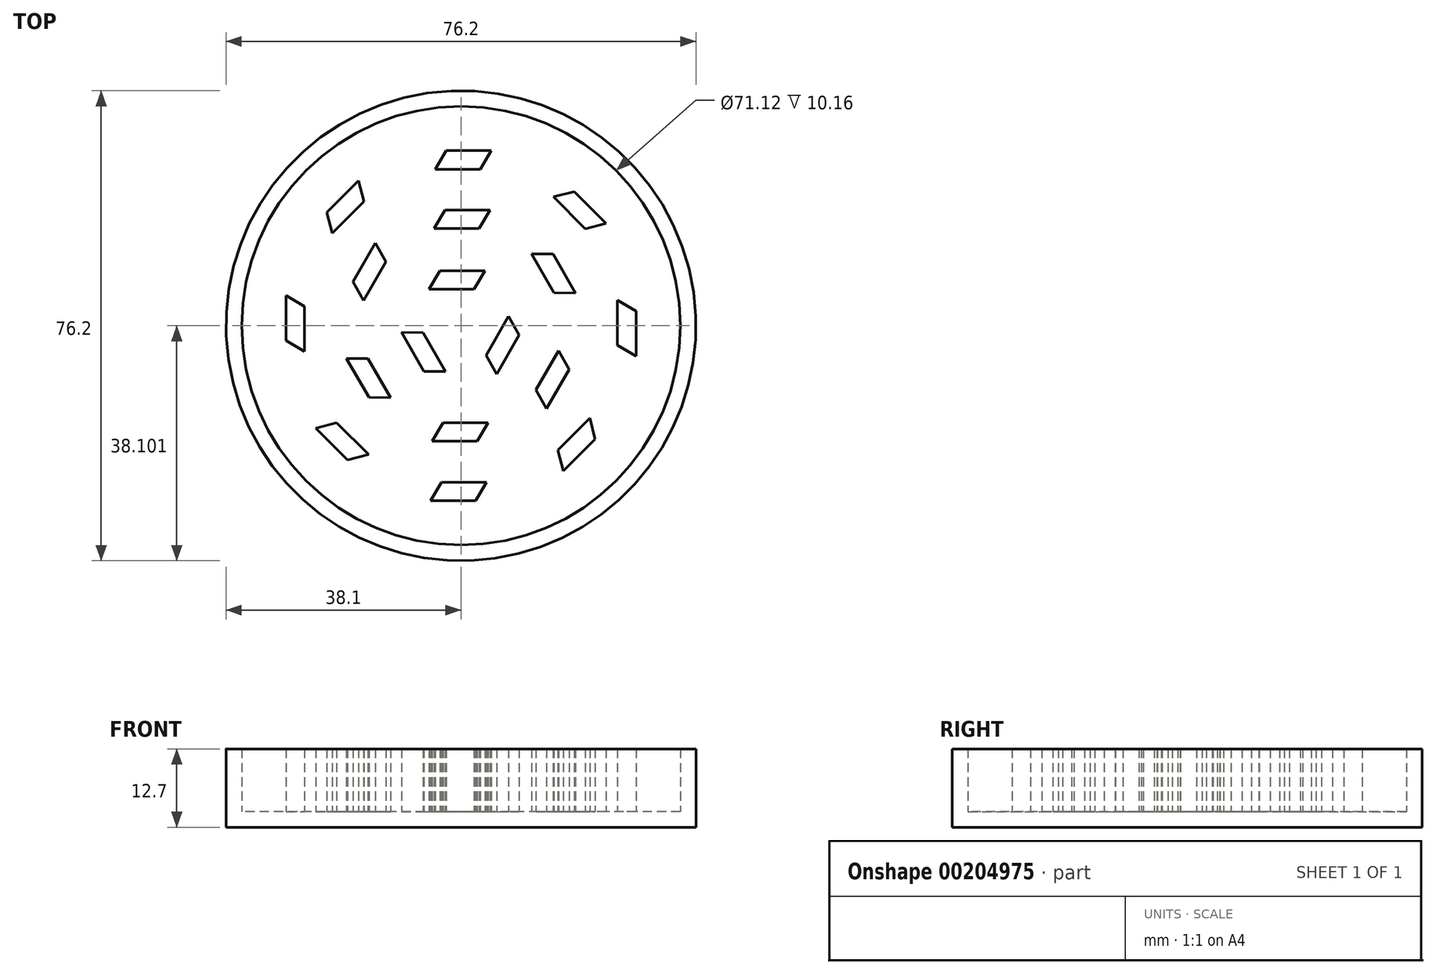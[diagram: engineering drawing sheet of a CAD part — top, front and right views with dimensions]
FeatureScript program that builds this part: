
annotation { "Feature Type Name" : "Feature", "Feature Type Description" : "" }
export const myFeature = defineFeature(function(context is Context, id is Id, definition is map)
    precondition{}
    {
        {
            var Q0;
            Q0=qCreatedBy(makeId("Top.planeOp"),FACE);
            var sketch = newSketch(context, id + "F0", { "sketchPlane" : qUnion([Q0])});
            skCircle(sketch, "E0", {"center": v(0, 0) * mm, "radius": 38.1 * mm});
            skSolve(sketch);
        }
        {
            var Q0;
            Q0=makeQuery(id+"F0.imprint","IMPRINT",FACE,{"disambiguationData":[TD([[makeQuery(id+"F0.imprint","IMPRINT",EDGE,{"derivedFrom":sQuery(id+"F0.wireOp",EDGE,"E0")}),1.0]])]});
            extrude(context, id + "F1", {"entities" : qUnion([Q0]), "oppositeDirection" : true, "depth" : 2.54 * mm});
        }
        {
            var Q0;
            Q0=makeQuery(id+"F1.opExtrude","CAP_FACE",FACE,{"disambiguationData":[OSD([sQuery(id+"F0.wireOp",EDGE,"E0")])],"isStart":true});
            var sketch = newSketch(context, id + "F2", { "sketchPlane" : qUnion([Q0])});
            skCircle(sketch, "E1", {"center": v(0, 0) * mm, "radius": 38.1 * mm});
            skCircle(sketch, "E2", {"center": v(0, 0) * mm, "radius": 35.56 * mm});
            skCircle(sketch, "E3", {"center": v(0, 0) * mm, "radius": 1.65 * mm});
            skCircle(sketch, "E4.cCircle", {"center": v(0, 0) * mm, "radius": 2.43 * mm, "construction": true});
            skPoint(sketch, "E4.0.midPoint", {"position": v(2.1, -1.21) * mm});
            skCircle(sketch, "E5", {"center": v(0, 0) * mm, "radius": 5.8 * mm, "construction": true});
            skCircle(sketch, "E6.0", {"center": v(0, 0) * mm, "radius": 9.86 * mm, "construction": true});
            skCircle(sketch, "E7.0", {"center": v(0, 0) * mm, "radius": 33.02 * mm});
            skCircle(sketch, "E8.0", {"center": v(0, 0) * mm, "radius": 10.62 * mm, "construction": true});
            skCircle(sketch, "E9.0", {"center": v(0, 0) * mm, "radius": 14.69 * mm, "construction": true});
            skCircle(sketch, "E10.0", {"center": v(0, 0) * mm, "radius": 15.45 * mm, "construction": true});
            skCircle(sketch, "E11.0", {"center": v(0, 0) * mm, "radius": 19.51 * mm, "construction": true});
            skCircle(sketch, "E12.0", {"center": v(0, 0) * mm, "radius": 20.27 * mm, "construction": true});
            skCircle(sketch, "E13.0", {"center": v(0, 0) * mm, "radius": 24.34 * mm, "construction": true});
            skCircle(sketch, "E14.0", {"center": v(0, 0) * mm, "radius": 25.1 * mm, "construction": true});
            skCircle(sketch, "E15.0", {"center": v(0, 0) * mm, "radius": 29.16 * mm, "construction": true});
            skCircle(sketch, "E16.0", {"center": v(0, 0) * mm, "radius": 29.93 * mm, "construction": true});
            skLineSegment(sketch, "E17.2.0", {"start": v(2.12, 5.9) * mm, "end": v(-5.18, 5.9) * mm});
            skLineSegment(sketch, "E17.2.1", {"start": v(3.9, 8.9) * mm, "end": v(2.12, 5.9) * mm});
            skLineSegment(sketch, "E17.2.2", {"start": v(3.9, 8.9) * mm, "end": v(-3.4, 8.9) * mm});
            skLineSegment(sketch, "E17.2.3", {"start": v(-3.4, 8.9) * mm, "end": v(-5.18, 5.9) * mm});
            skLineSegment(sketch, "E18.1.0", {"start": v(-9.66, -1.08) * mm, "end": v(-6.17, -1.11) * mm});
            skLineSegment(sketch, "E18.1.1", {"start": v(-6.17, -1.11) * mm, "end": v(-2.52, -7.44) * mm});
            skLineSegment(sketch, "E18.1.2", {"start": v(-6.01, -7.4) * mm, "end": v(-2.52, -7.44) * mm});
            skLineSegment(sketch, "E18.1.3", {"start": v(-9.66, -1.08) * mm, "end": v(-6.01, -7.4) * mm});
            skLineSegment(sketch, "E18.2.0", {"start": v(5.77, -7.83) * mm, "end": v(4.05, -4.79) * mm});
            skLineSegment(sketch, "E18.2.1", {"start": v(4.05, -4.79) * mm, "end": v(7.7, 1.53) * mm});
            skLineSegment(sketch, "E18.2.2", {"start": v(9.42, -1.5) * mm, "end": v(7.7, 1.53) * mm});
            skLineSegment(sketch, "E18.2.3", {"start": v(5.77, -7.83) * mm, "end": v(9.42, -1.5) * mm});
            skLineSegment(sketch, "E19.2.0", {"start": v(2.92, 15.74) * mm, "end": v(-4.38, 15.74) * mm});
            skLineSegment(sketch, "E19.2.1", {"start": v(4.7, 18.74) * mm, "end": v(2.92, 15.74) * mm});
            skLineSegment(sketch, "E19.2.2", {"start": v(4.7, 18.74) * mm, "end": v(-2.6, 18.74) * mm});
            skLineSegment(sketch, "E19.2.3", {"start": v(-2.6, 18.74) * mm, "end": v(-4.38, 15.74) * mm});
            skLineSegment(sketch, "E20.1.0", {"start": v(-13.88, 13.44) * mm, "end": v(-12.17, 10.4) * mm});
            skLineSegment(sketch, "E20.1.1", {"start": v(-13.88, 13.44) * mm, "end": v(-17.54, 7.11) * mm});
            skLineSegment(sketch, "E20.1.2", {"start": v(-12.17, 10.4) * mm, "end": v(-15.82, 4.07) * mm});
            skLineSegment(sketch, "E20.1.3", {"start": v(-17.54, 7.11) * mm, "end": v(-15.82, 4.07) * mm});
            skLineSegment(sketch, "E20.2.0", {"start": v(-18.58, -5.3) * mm, "end": v(-15.09, -5.34) * mm});
            skLineSegment(sketch, "E20.2.1", {"start": v(-18.58, -5.3) * mm, "end": v(-14.93, -11.63) * mm});
            skLineSegment(sketch, "E20.2.2", {"start": v(-15.09, -5.34) * mm, "end": v(-11.44, -11.66) * mm});
            skLineSegment(sketch, "E20.2.3", {"start": v(-14.93, -11.63) * mm, "end": v(-11.44, -11.66) * mm});
            skLineSegment(sketch, "E20.3.0", {"start": v(-4.7, -18.74) * mm, "end": v(-2.92, -15.74) * mm});
            skLineSegment(sketch, "E20.3.1", {"start": v(-4.7, -18.74) * mm, "end": v(2.6, -18.74) * mm});
            skLineSegment(sketch, "E20.3.2", {"start": v(-2.92, -15.74) * mm, "end": v(4.38, -15.74) * mm});
            skLineSegment(sketch, "E20.3.3", {"start": v(2.6, -18.74) * mm, "end": v(4.38, -15.74) * mm});
            skLineSegment(sketch, "E20.4.0", {"start": v(13.88, -13.44) * mm, "end": v(12.17, -10.4) * mm});
            skLineSegment(sketch, "E20.4.1", {"start": v(13.88, -13.44) * mm, "end": v(17.54, -7.11) * mm});
            skLineSegment(sketch, "E20.4.2", {"start": v(12.17, -10.4) * mm, "end": v(15.82, -4.07) * mm});
            skLineSegment(sketch, "E20.4.3", {"start": v(17.54, -7.11) * mm, "end": v(15.82, -4.07) * mm});
            skLineSegment(sketch, "E20.5.0", {"start": v(18.58, 5.3) * mm, "end": v(15.09, 5.34) * mm});
            skLineSegment(sketch, "E20.5.1", {"start": v(18.58, 5.3) * mm, "end": v(14.93, 11.63) * mm});
            skLineSegment(sketch, "E20.5.2", {"start": v(15.09, 5.34) * mm, "end": v(11.44, 11.66) * mm});
            skLineSegment(sketch, "E20.5.3", {"start": v(14.93, 11.63) * mm, "end": v(11.44, 11.66) * mm});
            skLineSegment(sketch, "E21.2.0", {"start": v(3.13, 25.38) * mm, "end": v(-4.17, 25.38) * mm});
            skLineSegment(sketch, "E21.2.1", {"start": v(4.9, 28.38) * mm, "end": v(3.13, 25.38) * mm});
            skLineSegment(sketch, "E21.2.2", {"start": v(4.9, 28.38) * mm, "end": v(-2.4, 28.38) * mm});
            skLineSegment(sketch, "E21.2.3", {"start": v(-2.4, 28.38) * mm, "end": v(-4.17, 25.38) * mm});
            skLineSegment(sketch, "E22.1.0", {"start": v(-15.73, 20.16) * mm, "end": v(-20.9, 15) * mm});
            skLineSegment(sketch, "E22.1.1", {"start": v(-16.6, 23.54) * mm, "end": v(-15.73, 20.16) * mm});
            skLineSegment(sketch, "E22.1.2", {"start": v(-16.6, 23.54) * mm, "end": v(-21.76, 18.38) * mm});
            skLineSegment(sketch, "E22.1.3", {"start": v(-21.76, 18.38) * mm, "end": v(-20.9, 15) * mm});
            skLineSegment(sketch, "E22.2.0", {"start": v(-25.38, 3.13) * mm, "end": v(-25.38, -4.17) * mm});
            skLineSegment(sketch, "E22.2.1", {"start": v(-28.38, 4.9) * mm, "end": v(-25.38, 3.13) * mm});
            skLineSegment(sketch, "E22.2.2", {"start": v(-28.38, 4.9) * mm, "end": v(-28.38, -2.4) * mm});
            skLineSegment(sketch, "E22.2.3", {"start": v(-28.38, -2.4) * mm, "end": v(-25.38, -4.17) * mm});
            skLineSegment(sketch, "E22.3.0", {"start": v(-20.16, -15.73) * mm, "end": v(-15, -20.9) * mm});
            skLineSegment(sketch, "E22.3.1", {"start": v(-23.54, -16.6) * mm, "end": v(-20.16, -15.73) * mm});
            skLineSegment(sketch, "E22.3.2", {"start": v(-23.54, -16.6) * mm, "end": v(-18.38, -21.76) * mm});
            skLineSegment(sketch, "E22.3.3", {"start": v(-18.38, -21.76) * mm, "end": v(-15, -20.9) * mm});
            skLineSegment(sketch, "E22.4.0", {"start": v(-3.13, -25.38) * mm, "end": v(4.17, -25.38) * mm});
            skLineSegment(sketch, "E22.4.1", {"start": v(-4.9, -28.38) * mm, "end": v(-3.13, -25.38) * mm});
            skLineSegment(sketch, "E22.4.2", {"start": v(-4.9, -28.38) * mm, "end": v(2.4, -28.38) * mm});
            skLineSegment(sketch, "E22.4.3", {"start": v(2.4, -28.38) * mm, "end": v(4.17, -25.38) * mm});
            skLineSegment(sketch, "E22.5.0", {"start": v(15.73, -20.16) * mm, "end": v(20.9, -15) * mm});
            skLineSegment(sketch, "E22.5.1", {"start": v(16.6, -23.54) * mm, "end": v(15.73, -20.16) * mm});
            skLineSegment(sketch, "E22.5.2", {"start": v(16.6, -23.54) * mm, "end": v(21.76, -18.38) * mm});
            skLineSegment(sketch, "E22.5.3", {"start": v(21.76, -18.38) * mm, "end": v(20.9, -15) * mm});
            skLineSegment(sketch, "E22.6.0", {"start": v(25.38, -3.13) * mm, "end": v(25.38, 4.17) * mm});
            skLineSegment(sketch, "E22.6.1", {"start": v(28.38, -4.9) * mm, "end": v(25.38, -3.13) * mm});
            skLineSegment(sketch, "E22.6.2", {"start": v(28.38, -4.9) * mm, "end": v(28.38, 2.4) * mm});
            skLineSegment(sketch, "E22.6.3", {"start": v(28.38, 2.4) * mm, "end": v(25.38, 4.17) * mm});
            skLineSegment(sketch, "E22.7.0", {"start": v(20.16, 15.73) * mm, "end": v(15, 20.9) * mm});
            skLineSegment(sketch, "E22.7.1", {"start": v(23.54, 16.6) * mm, "end": v(20.16, 15.73) * mm});
            skLineSegment(sketch, "E22.7.2", {"start": v(23.54, 16.6) * mm, "end": v(18.38, 21.76) * mm});
            skLineSegment(sketch, "E22.7.3", {"start": v(18.38, 21.76) * mm, "end": v(15, 20.9) * mm});
            skSolve(sketch);
        }
        {
            var Q0;
            Q0=makeQuery(id+"F2.imprint","IMPRINT",FACE,{"disambiguationData":[TD([[makeQuery(id+"F2.imprint","IMPRINT",EDGE,{"derivedFrom":sQuery(id+"F2.wireOp",EDGE,"E2")}),-1.0]])]});
            var Q1;
            Q1=makeQuery(id+"F2.imprint","IMPRINT",FACE,{"disambiguationData":[TD([[makeQuery(id+"F2.imprint","IMPRINT",EDGE,{"derivedFrom":sQuery(id+"F2.wireOp",EDGE,"E21.2.0")}),-1.0]])]});
            var Q2;
            Q2=makeQuery(id+"F2.imprint","IMPRINT",FACE,{"disambiguationData":[TD([[makeQuery(id+"F2.imprint","IMPRINT",EDGE,{"derivedFrom":sQuery(id+"F2.wireOp",EDGE,"E22.7.0")}),-1.0]])]});
            var Q3;
            Q3=makeQuery(id+"F2.imprint","IMPRINT",FACE,{"disambiguationData":[TD([[makeQuery(id+"F2.imprint","IMPRINT",EDGE,{"derivedFrom":sQuery(id+"F2.wireOp",EDGE,"E22.6.0")}),-1.0]])]});
            var Q4;
            Q4=makeQuery(id+"F2.imprint","IMPRINT",FACE,{"disambiguationData":[TD([[makeQuery(id+"F2.imprint","IMPRINT",EDGE,{"derivedFrom":sQuery(id+"F2.wireOp",EDGE,"E20.5.0")}),-1.0]])]});
            var Q5;
            Q5=makeQuery(id+"F2.imprint","IMPRINT",FACE,{"disambiguationData":[TD([[makeQuery(id+"F2.imprint","IMPRINT",EDGE,{"derivedFrom":sQuery(id+"F2.wireOp",EDGE,"E19.2.0")}),-1.0]])]});
            var Q6;
            Q6=makeQuery(id+"F2.imprint","IMPRINT",FACE,{"disambiguationData":[TD([[makeQuery(id+"F2.imprint","IMPRINT",EDGE,{"derivedFrom":sQuery(id+"F2.wireOp",EDGE,"E22.1.0")}),-1.0]])]});
            var Q7;
            Q7=makeQuery(id+"F2.imprint","IMPRINT",FACE,{"disambiguationData":[TD([[makeQuery(id+"F2.imprint","IMPRINT",EDGE,{"derivedFrom":sQuery(id+"F2.wireOp",EDGE,"E20.1.0")}),-1.0]])]});
            var Q8;
            Q8=makeQuery(id+"F2.imprint","IMPRINT",FACE,{"disambiguationData":[TD([[makeQuery(id+"F2.imprint","IMPRINT",EDGE,{"derivedFrom":sQuery(id+"F2.wireOp",EDGE,"E17.2.0")}),-1.0]])]});
            var Q9;
            Q9=makeQuery(id+"F2.imprint","IMPRINT",FACE,{"disambiguationData":[TD([[makeQuery(id+"F2.imprint","IMPRINT",EDGE,{"derivedFrom":sQuery(id+"F2.wireOp",EDGE,"E22.2.0")}),-1.0]])]});
            var Q10;
            Q10=makeQuery(id+"F2.imprint","IMPRINT",FACE,{"disambiguationData":[TD([[makeQuery(id+"F2.imprint","IMPRINT",EDGE,{"derivedFrom":sQuery(id+"F2.wireOp",EDGE,"E20.2.0")}),-1.0]])]});
            var Q11;
            Q11=makeQuery(id+"F2.imprint","IMPRINT",FACE,{"disambiguationData":[TD([[makeQuery(id+"F2.imprint","IMPRINT",EDGE,{"derivedFrom":sQuery(id+"F2.wireOp",EDGE,"E18.1.0")}),-1.0]])]});
            var Q12;
            Q12=makeQuery(id+"F2.imprint","IMPRINT",FACE,{"disambiguationData":[TD([[makeQuery(id+"F2.imprint","IMPRINT",EDGE,{"derivedFrom":sQuery(id+"F2.wireOp",EDGE,"E18.2.0")}),-1.0]])]});
            var Q13;
            Q13=makeQuery(id+"F2.imprint","IMPRINT",FACE,{"disambiguationData":[TD([[makeQuery(id+"F2.imprint","IMPRINT",EDGE,{"derivedFrom":sQuery(id+"F2.wireOp",EDGE,"E20.4.0")}),-1.0]])]});
            var Q14;
            Q14=makeQuery(id+"F2.imprint","IMPRINT",FACE,{"disambiguationData":[TD([[makeQuery(id+"F2.imprint","IMPRINT",EDGE,{"derivedFrom":sQuery(id+"F2.wireOp",EDGE,"E22.5.0")}),-1.0]])]});
            var Q15;
            Q15=makeQuery(id+"F2.imprint","IMPRINT",FACE,{"disambiguationData":[TD([[makeQuery(id+"F2.imprint","IMPRINT",EDGE,{"derivedFrom":sQuery(id+"F2.wireOp",EDGE,"E20.3.0")}),-1.0]])]});
            var Q16;
            Q16=makeQuery(id+"F2.imprint","IMPRINT",FACE,{"disambiguationData":[TD([[makeQuery(id+"F2.imprint","IMPRINT",EDGE,{"derivedFrom":sQuery(id+"F2.wireOp",EDGE,"E22.3.0")}),-1.0]])]});
            var Q17;
            Q17=makeQuery(id+"F2.imprint","IMPRINT",FACE,{"disambiguationData":[TD([[makeQuery(id+"F2.imprint","IMPRINT",EDGE,{"derivedFrom":sQuery(id+"F2.wireOp",EDGE,"E22.4.0")}),-1.0]])]});
            extrude(context, id + "F3", {"entities" : qUnion([Q0, Q1, Q2, Q3, Q4, Q5, Q6, Q7, Q8, Q9, Q10, Q11, Q12, Q13, Q14, Q15, Q16, Q17]), "operationType" : NewBodyOperationType.ADD, "depth" : 10.16 * mm});
        }
    });
